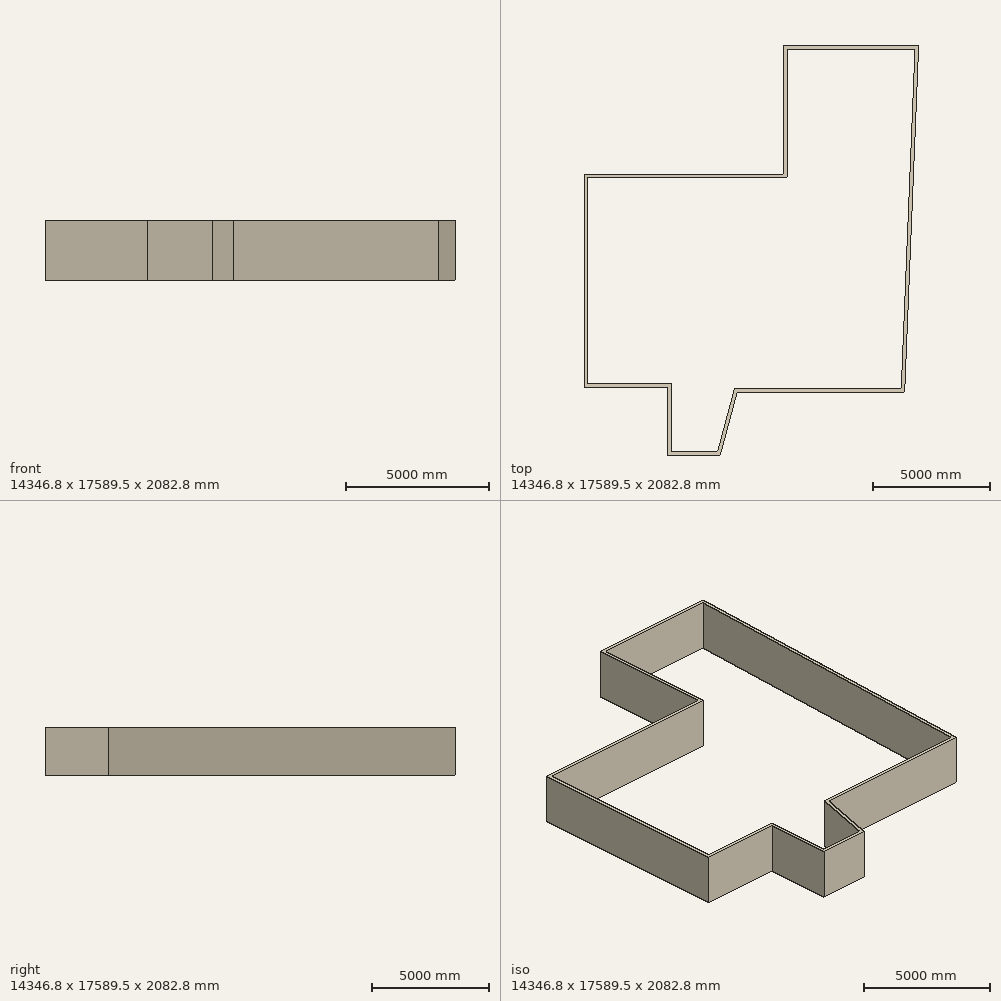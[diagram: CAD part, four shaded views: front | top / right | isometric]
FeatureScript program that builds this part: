
annotation { "Feature Type Name" : "Feature", "Feature Type Description" : "" }
export const myFeature = defineFeature(function(context is Context, id is Id, definition is map)
    precondition{}
    {
        {
            var Q0;
            Q0=qCreatedBy(makeId("Top.planeOp"),FACE);
            var sketch = newSketch(context, id + "F0", { "sketchPlane" : qUnion([Q0])});
            skLineSegment(sketch, "E0", {"start": v(0, 0) * mm, "end": v(0, 9144) * mm});
            skLineSegment(sketch, "E1", {"start": v(0, 9144) * mm, "end": v(8550.56, 9144) * mm});
            skLineSegment(sketch, "E2", {"start": v(8550.56, 9144) * mm, "end": v(8550.56, 14659.16) * mm});
            skLineSegment(sketch, "E3", {"start": v(8550.56, 14659.16) * mm, "end": v(14346.8, 14659.16) * mm});
            skLineSegment(sketch, "E4", {"start": v(14346.8, 14659.16) * mm, "end": v(13744.92, -211.69) * mm});
            skLineSegment(sketch, "E5", {"start": v(13744.92, -211.69) * mm, "end": v(6567.14, -211.69) * mm});
            skLineSegment(sketch, "E6", {"start": v(6567.14, -211.69) * mm, "end": v(5835.8, -2930.32) * mm});
            skLineSegment(sketch, "E7", {"start": v(5835.8, -2930.32) * mm, "end": v(3574.34, -2930.32) * mm});
            skLineSegment(sketch, "E8", {"start": v(3574.34, -2930.32) * mm, "end": v(3574.34, 0) * mm});
            skLineSegment(sketch, "E9", {"start": v(3574.34, 0) * mm, "end": v(0, 0) * mm});
            skLineSegment(sketch, "E10.0", {"start": v(3726.74, 152.4) * mm, "end": v(152.4, 152.4) * mm});
            skLineSegment(sketch, "E10.1", {"start": v(3726.74, -2777.92) * mm, "end": v(3726.74, 152.4) * mm});
            skLineSegment(sketch, "E10.2", {"start": v(152.4, 152.4) * mm, "end": v(152.4, 8991.6) * mm});
            skLineSegment(sketch, "E10.3", {"start": v(5718.99, -2777.92) * mm, "end": v(3726.74, -2777.92) * mm});
            skLineSegment(sketch, "E10.4", {"start": v(6450.32, -59.29) * mm, "end": v(5718.99, -2777.92) * mm});
            skLineSegment(sketch, "E10.5", {"start": v(13598.57, -59.29) * mm, "end": v(6450.32, -59.29) * mm});
            skLineSegment(sketch, "E10.6", {"start": v(152.4, 8991.6) * mm, "end": v(8702.96, 8991.6) * mm});
            skLineSegment(sketch, "E10.7", {"start": v(8702.96, 8991.6) * mm, "end": v(8702.96, 14506.76) * mm});
            skLineSegment(sketch, "E10.8", {"start": v(8702.96, 14506.76) * mm, "end": v(14188.1, 14506.76) * mm});
            skLineSegment(sketch, "E10.9", {"start": v(14188.1, 14506.76) * mm, "end": v(13598.57, -59.29) * mm});
            skSolve(sketch);
        }
        {
            var Q0;
            Q0=makeQuery(id+"F0.imprint","IMPRINT",FACE,{"disambiguationData":[TD([[makeQuery(id+"F0.imprint","IMPRINT",EDGE,{"derivedFrom":sQuery(id+"F0.wireOp",EDGE,"E0")}),-1.0]])]});
            extrude(context, id + "F1", {"entities" : qUnion([Q0]), "depth" : 2082.8 * mm, "offsetDistance" : 25.4 * mm});
        }
    });
